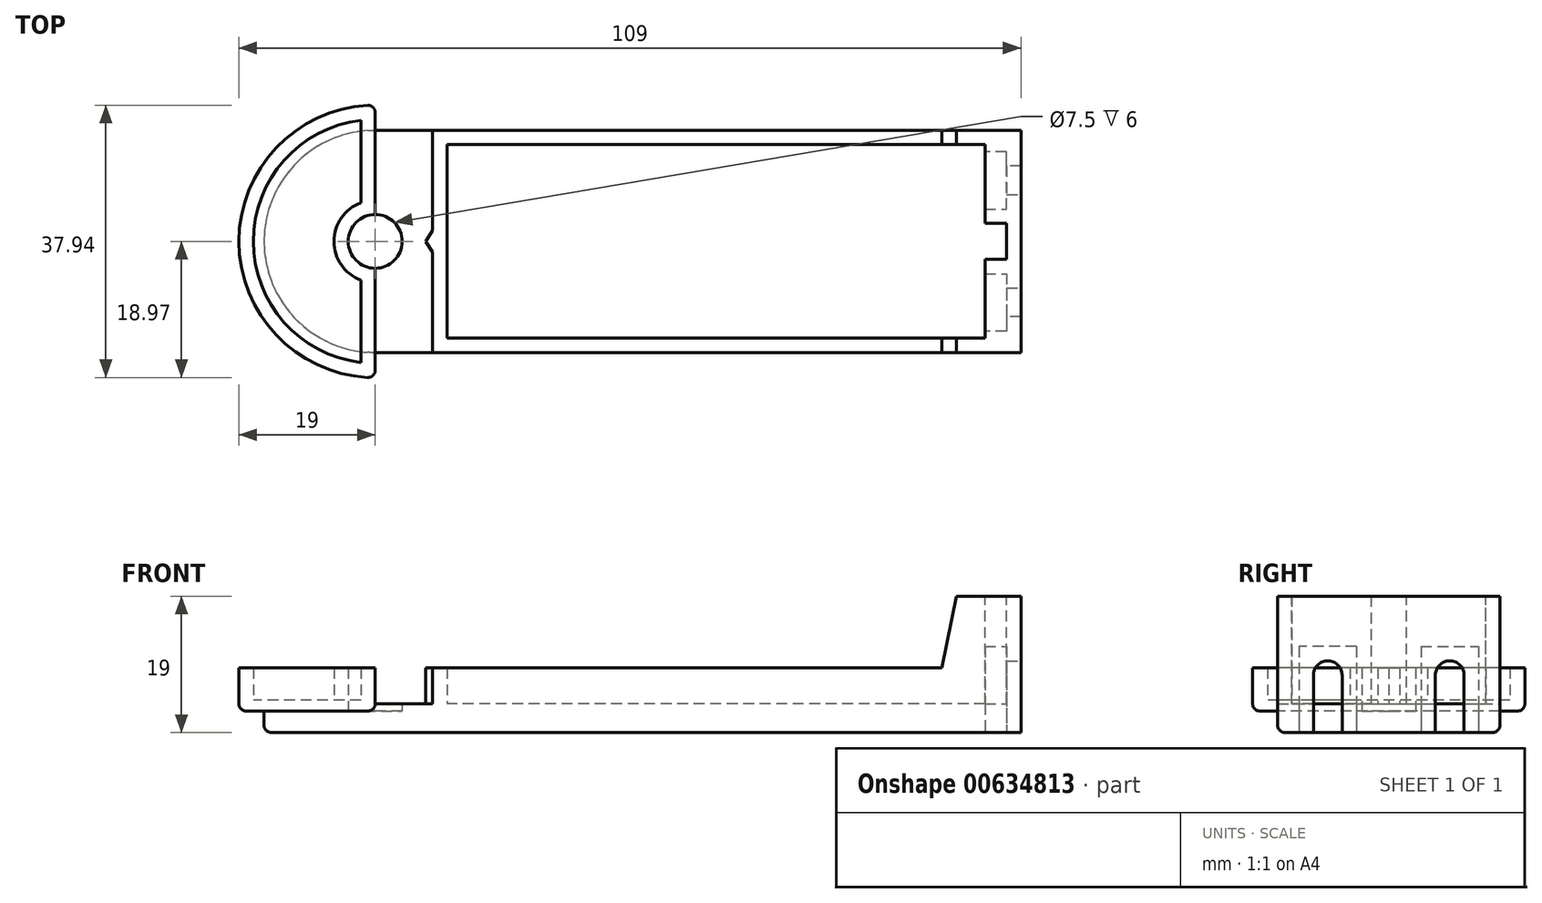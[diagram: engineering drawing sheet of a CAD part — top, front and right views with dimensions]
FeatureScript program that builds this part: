
annotation { "Feature Type Name" : "Feature", "Feature Type Description" : "" }
export const myFeature = defineFeature(function(context is Context, id is Id, definition is map)
    precondition{}
    {
        {
            var Q0;
            Q0=qCreatedBy(makeId("Top.planeOp"),FACE);
            var sketch = newSketch(context, id + "F0", { "sketchPlane" : qUnion([Q0])});
            skCircle(sketch, "E0", {"center": v(0, 0) * mm, "radius": 15.5 * mm});
            skLineSegment(sketch, "E1.bottom", {"start": v(0, 15.5) * mm, "end": v(90, 15.5) * mm});
            skLineSegment(sketch, "E1.top", {"start": v(0, -15.5) * mm, "end": v(90, -15.5) * mm});
            skLineSegment(sketch, "E1.left", {"start": v(0, 15.5) * mm, "end": v(0, -15.5) * mm});
            skLineSegment(sketch, "E1.right", {"start": v(90, 15.5) * mm, "end": v(90, -15.5) * mm});
            skSolve(sketch);
        }
        {
            var Q0;
            Q0 = qSketchRegion(id + "F0", true);
            extrude(context, id + "F1", {"entities" : qUnion([Q0]), "depth" : 4 * mm, "offsetDistance" : 25 * mm});
        }
        {
            var Q0;
            Q0=makeQuery(id+"F1.opExtrude","CAP_FACE",FACE,{"disambiguationData":[OSD([sQuery(id+"F0.wireOp",EDGE,"E0"),sQuery(id+"F0.wireOp",EDGE,"E1.bottom"),sQuery(id+"F0.wireOp",EDGE,"E1.top"),sQuery(id+"F0.wireOp",EDGE,"E1.right")])],"isStart":false});
            var sketch = newSketch(context, id + "F2", { "sketchPlane" : qUnion([Q0])});
            skLineSegment(sketch, "E2.top", {"start": v(90, 15.5) * mm, "end": v(8, 15.5) * mm});
            skLineSegment(sketch, "E2.left", {"start": v(90, -15.5) * mm, "end": v(90, 15.5) * mm});
            skLineSegment(sketch, "E3.0", {"start": v(88, 13.5) * mm, "end": v(10, 13.5) * mm});
            skLineSegment(sketch, "E4.0", {"start": v(88, -13.5) * mm, "end": v(88, 13.5) * mm});
            skLineSegment(sketch, "E5", {"start": v(90, -15.5) * mm, "end": v(8, -15.5) * mm});
            skLineSegment(sketch, "E6", {"start": v(10, -13.5) * mm, "end": v(88, -13.5) * mm});
            skLineSegment(sketch, "E7", {"start": v(8, -15.5) * mm, "end": v(8, 15.5) * mm});
            skLineSegment(sketch, "E8.0", {"start": v(10, -13.5) * mm, "end": v(10, 13.5) * mm});
            skSolve(sketch);
        }
        {
            var Q0;
            Q0 = qSketchRegion(id + "F2", true);
            extrude(context, id + "F3", {"entities" : qUnion([Q0]), "operationType" : NewBodyOperationType.ADD, "depth" : 15 * mm, "offsetDistance" : 25 * mm});
        }
        {
            var Q0;
            Q0=makeQuery(id+"F3.boolean.opBoolean","MERGE",FACE,{"derivedFrom":[makeQuery(id+"F1.opExtrude","SWEPT_FACE",FACE,{"disambiguationData":[OSD([sQuery(id+"F0.wireOp",EDGE,"E1.top")])]}),makeQuery(id+"F3.opExtrude","SWEPT_FACE",FACE,{"disambiguationData":[OSD([sQuery(id+"F2.wireOp",EDGE,"E2.bottom")])]})]});
            var sketch = newSketch(context, id + "F4", { "sketchPlane" : qUnion([Q0])});
            skLineSegment(sketch, "E9", {"start": v(79, 9) * mm, "end": v(81, 19) * mm});
            skLineSegment(sketch, "E10", {"start": v(8, 9) * mm, "end": v(8, 19) * mm});
            skLineSegment(sketch, "E11", {"start": v(81, 19) * mm, "end": v(8, 19) * mm});
            skLineSegment(sketch, "E12", {"start": v(8, 9) * mm, "end": v(79, 9) * mm});
            skSolve(sketch);
        }
        {
            var Q0;
            Q0 = qSketchRegion(id + "F4", true);
            extrude(context, id + "F5", {"entities" : qUnion([Q0]), "operationType" : NewBodyOperationType.REMOVE, "oppositeDirection" : true, "depth" : 31 * mm, "offsetDistance" : 25 * mm});
        }
        {
            var Q0;
            Q0=makeQuery(id+"F1.opExtrude","CAP_FACE",FACE,{"disambiguationData":[OSD([sQuery(id+"F0.wireOp",EDGE,"E0"),sQuery(id+"F0.wireOp",EDGE,"E1.bottom"),sQuery(id+"F0.wireOp",EDGE,"E1.top"),sQuery(id+"F0.wireOp",EDGE,"E1.right")])],"isStart":true});
            var sketch = newSketch(context, id + "F6", { "sketchPlane" : qUnion([Q0])});
            skLineSegment(sketch, "E13.bottom", {"start": v(90, 15.5) * mm, "end": v(85, 15.5) * mm});
            skLineSegment(sketch, "E13.top", {"start": v(90, 2.5) * mm, "end": v(85, 2.5) * mm});
            skLineSegment(sketch, "E13.left", {"start": v(90, 15.5) * mm, "end": v(90, 2.5) * mm});
            skLineSegment(sketch, "E13.right", {"start": v(85, 15.5) * mm, "end": v(85, 2.5) * mm});
            skLineSegment(sketch, "E14.bottom", {"start": v(90, -15.5) * mm, "end": v(85, -15.5) * mm});
            skLineSegment(sketch, "E14.top", {"start": v(90, -2.5) * mm, "end": v(85, -2.5) * mm});
            skLineSegment(sketch, "E14.left", {"start": v(90, -15.5) * mm, "end": v(90, -2.5) * mm});
            skLineSegment(sketch, "E14.right", {"start": v(85, -15.5) * mm, "end": v(85, -2.5) * mm});
            skSolve(sketch);
        }
        {
            var Q0;
            Q0 = qSketchRegion(id + "F6", true);
            extrude(context, id + "F7", {"entities" : qUnion([Q0]), "operationType" : NewBodyOperationType.ADD, "oppositeDirection" : true, "depth" : 19 * mm, "offsetDistance" : 25 * mm});
        }
        {
            var Q0;
            Q0=makeQuery(id+"F1.opExtrude","CAP_FACE",FACE,{"disambiguationData":[OSD([sQuery(id+"F0.wireOp",EDGE,"E0"),sQuery(id+"F0.wireOp",EDGE,"E1.bottom"),sQuery(id+"F0.wireOp",EDGE,"E1.top"),sQuery(id+"F0.wireOp",EDGE,"E1.right")])],"isStart":true});
            var sketch = newSketch(context, id + "F8", { "sketchPlane" : qUnion([Q0])});
            skLineSegment(sketch, "E15", {"start": v(90, -15.5) * mm, "end": v(90, -10.5) * mm});
            skLineSegment(sketch, "E16", {"start": v(90, -10.5) * mm, "end": v(88, -10.5) * mm});
            skLineSegment(sketch, "E17", {"start": v(88, -10.5) * mm, "end": v(88, -12.5) * mm});
            skLineSegment(sketch, "E18", {"start": v(88, -12.5) * mm, "end": v(85, -12.5) * mm});
            skLineSegment(sketch, "E19", {"start": v(85, -12.5) * mm, "end": v(85, -4.5) * mm});
            skLineSegment(sketch, "E20", {"start": v(85, -4.5) * mm, "end": v(88, -4.5) * mm});
            skLineSegment(sketch, "E21", {"start": v(88, -4.5) * mm, "end": v(88, -6.5) * mm});
            skLineSegment(sketch, "E22", {"start": v(88, -6.5) * mm, "end": v(90, -6.5) * mm});
            skLineSegment(sketch, "E23", {"start": v(90, -6.5) * mm, "end": v(90, -10.5) * mm});
            skLineSegment(sketch, "E24", {"start": v(0, 0) * mm, "end": v(90, 0) * mm, "construction": true});
            skLineSegment(sketch, "E25.MirrorCS", {"start": v(90, 6.5) * mm, "end": v(90, 10.5) * mm});
            skLineSegment(sketch, "E26.MirrorCS", {"start": v(88, 6.5) * mm, "end": v(90, 6.5) * mm});
            skLineSegment(sketch, "E27.MirrorCS", {"start": v(90, 15.5) * mm, "end": v(90, 10.5) * mm});
            skLineSegment(sketch, "E28.MirrorCS", {"start": v(88, 4.5) * mm, "end": v(88, 6.5) * mm});
            skLineSegment(sketch, "E29.MirrorCS", {"start": v(90, 10.5) * mm, "end": v(88, 10.5) * mm});
            skLineSegment(sketch, "E30.MirrorCS", {"start": v(88, 12.5) * mm, "end": v(85, 12.5) * mm});
            skLineSegment(sketch, "E31.MirrorCS", {"start": v(88, 10.5) * mm, "end": v(88, 12.5) * mm});
            skLineSegment(sketch, "E32.MirrorCS", {"start": v(85, 4.5) * mm, "end": v(88, 4.5) * mm});
            skLineSegment(sketch, "E33.MirrorCS", {"start": v(85, 12.5) * mm, "end": v(85, 4.5) * mm});
            skSolve(sketch);
        }
        {
            var Q0;
            Q0 = qSketchRegion(id + "F8", true);
            extrude(context, id + "F9", {"entities" : qUnion([Q0]), "operationType" : NewBodyOperationType.REMOVE, "oppositeDirection" : true, "depth" : 12 * mm, "offsetDistance" : 25 * mm});
        }
        {
            var Q0;
            Q0=makeQuery(id+"F3.boolean.opBoolean","MERGE",FACE,{"derivedFrom":[makeQuery(id+"F1.opExtrude","SWEPT_FACE",FACE,{"disambiguationData":[OSD([sQuery(id+"F0.wireOp",EDGE,"E1.right")])]}),makeQuery(id+"F3.opExtrude","SWEPT_FACE",FACE,{"disambiguationData":[OSD([sQuery(id+"F2.wireOp",EDGE,"E2.left")])]})]});
            var sketch = newSketch(context, id + "F10", { "sketchPlane" : qUnion([Q0])});
            skLineSegment(sketch, "E34.bottom", {"start": v(10.5, 12) * mm, "end": v(6.5, 12) * mm});
            skLineSegment(sketch, "E34.left", {"start": v(10.5, 12) * mm, "end": v(10.5, 8) * mm});
            skLineSegment(sketch, "E34.right", {"start": v(6.5, 12) * mm, "end": v(6.5, 8) * mm});
            skLineSegment(sketch, "E35.bottom", {"start": v(-6.5, 12) * mm, "end": v(-10.5, 12) * mm});
            skLineSegment(sketch, "E35.left", {"start": v(-6.5, 12) * mm, "end": v(-6.5, 8) * mm});
            skLineSegment(sketch, "E35.right", {"start": v(-10.5, 12) * mm, "end": v(-10.5, 8) * mm});
            skArc(sketch, "E36", {"start": v(10.5, 8) * mm, "mid": v(8.5, 10) * mm, "end": v(6.5, 8) * mm});
            skArc(sketch, "E37", {"start": v(-6.5, 8) * mm, "mid": v(-8.5, 10) * mm, "end": v(-10.5, 8) * mm});
            skSolve(sketch);
        }
        {
            var Q0;
            Q0 = qSketchRegion(id + "F10", true);
            extrude(context, id + "F11", {"entities" : qUnion([Q0]), "operationType" : NewBodyOperationType.ADD, "oppositeDirection" : true, "depth" : 2 * mm, "offsetDistance" : 25 * mm});
        }
        {
            var Q0;
            {var subQ0=sQuery(id+"F0.wireOp",EDGE,"E1.top");var subQ1=sQuery(id+"F0.wireOp",EDGE,"E1.bottom");var subQ2=sQuery(id+"F0.wireOp",EDGE,"E0");Q0=makeQuery(id+"F3.boolean.opBoolean","SPLIT",FACE,{"disambiguationData":[TD([makeQuery(id+"F1.opExtrude","SWEPT_FACE",FACE,{"disambiguationData":[OSD([subQ2])]})])],"derivedFrom":makeQuery(id+"F1.opExtrude","CAP_FACE",FACE,{"disambiguationData":[OSD([subQ2,subQ1,subQ0,sQuery(id+"F0.wireOp",EDGE,"E1.right")])],"isStart":false})});}
            var sketch = newSketch(context, id + "F12", { "sketchPlane" : qUnion([Q0])});
            skArc(sketch, "E38", {"start": v(0, 3.75) * mm, "mid": v(-3.75, 0) * mm, "end": v(0, -3.75) * mm});
            skArc(sketch, "E39", {"start": v(-2, 16.88) * mm, "mid": v(-17, 0) * mm, "end": v(-2, -16.88) * mm});
            skArc(sketch, "E40", {"start": v(-1.06, 18.97) * mm, "mid": v(-19, 0) * mm, "end": v(-1.06, -18.97) * mm});
            skArc(sketch, "E41", {"start": v(-2, 5.4) * mm, "mid": v(-5.75, 0) * mm, "end": v(-2, -5.4) * mm});
            skLineSegment(sketch, "E42", {"start": v(0, 17.97) * mm, "end": v(0, 3.75) * mm});
            skLineSegment(sketch, "E43.0", {"start": v(-2, 19) * mm, "end": v(-2, 18.9) * mm});
            skLineSegment(sketch, "E44.trimOffspring", {"start": v(-2, -18.9) * mm, "end": v(-2, -19) * mm});
            skLineSegment(sketch, "E45.trimOffspring", {"start": v(-2, 16.88) * mm, "end": v(-2, 5.4) * mm});
            skLineSegment(sketch, "E46.trimOffspring", {"start": v(-2, -5.4) * mm, "end": v(-2, -16.88) * mm});
            skLineSegment(sketch, "E47.trimOffspring", {"start": v(0, -3.75) * mm, "end": v(0, -17.97) * mm});
            skPoint(sketch, "E48.visualSharp", {"position": v(0, 19) * mm});
            skArc(sketch, "E48.filletArc", {"start": v(0, 17.97) * mm, "mid": v(-0.31, 18.7) * mm, "end": v(-1.06, 18.97) * mm});
            skPoint(sketch, "E49.visualSharp", {"position": v(0, -19) * mm});
            skArc(sketch, "E49.filletArc", {"start": v(-1.06, -18.97) * mm, "mid": v(-0.31, -18.7) * mm, "end": v(0, -17.97) * mm});
            skSolve(sketch);
        }
        {
            var Q0;
            Q0 = qSketchRegion(id + "F12", true);
            extrude(context, id + "F13", {"entities" : qUnion([Q0]), "operationType" : NewBodyOperationType.ADD, "depth" : 5 * mm, "offsetDistance" : 25 * mm, "hasSecondDirection" : true, "secondDirectionOppositeDirection" : true, "secondDirectionDepth" : 1 * mm});
        }
        {
            var Q0;
            {var subQ0=sQuery(id+"F12.wireOp",EDGE,"E41");var subQ3=sQuery(id+"F0.wireOp",EDGE,"E0");var subQ4=makeQuery(id+"F1.opExtrude","SWEPT_FACE",FACE,{"disambiguationData":[OSD([subQ3])]});var subQ5=sQuery(id+"F0.wireOp",EDGE,"E1.top");var subQ6=sQuery(id+"F0.wireOp",EDGE,"E1.bottom");Q0=makeQuery(id+"F13.boolean.opBoolean","SPLIT",FACE,{"disambiguationData":[TD([makeQuery(id+"F13.opExtrude","SWEPT_FACE",FACE,{"disambiguationData":[OSD([subQ0])]})])],"derivedFrom":makeQuery(id+"F3.boolean.opBoolean","SPLIT",FACE,{"disambiguationData":[TD([subQ4])],"derivedFrom":makeQuery(id+"F1.opExtrude","CAP_FACE",FACE,{"disambiguationData":[OSD([subQ3,subQ6,subQ5,sQuery(id+"F0.wireOp",EDGE,"E1.right")])],"isStart":false})})});}
            var sketch = newSketch(context, id + "F14", { "sketchPlane" : qUnion([Q0])});
            skLineSegment(sketch, "E50.0", {"start": v(-2.01, 19.14) * mm, "end": v(-2.01, 19.03) * mm});
            skLineSegment(sketch, "E51.trimOffspring", {"start": v(-2.01, -19.03) * mm, "end": v(-2.01, -19.14) * mm});
            skLineSegment(sketch, "E52.trimOffspring", {"start": v(0, 17) * mm, "end": v(0, 5.75) * mm});
            skLineSegment(sketch, "E53.trimOffspring", {"start": v(0, -5.75) * mm, "end": v(0, -17) * mm});
            skArc(sketch, "E54", {"start": v(0, 17) * mm, "mid": v(-17, 0) * mm, "end": v(0, -17) * mm});
            skArc(sketch, "E55", {"start": v(0, 5.75) * mm, "mid": v(-5.75, 0) * mm, "end": v(0, -5.75) * mm});
            skSolve(sketch);
        }
        {
            var Q0;
            Q0 = qSketchRegion(id + "F14", true);
            extrude(context, id + "F15", {"entities" : qUnion([Q0]), "operationType" : NewBodyOperationType.ADD, "depth" : 0.5 * mm, "offsetDistance" : 25 * mm, "hasSecondDirection" : true, "secondDirectionOppositeDirection" : true, "secondDirectionDepth" : 1 * mm});
        }
        {
            var Q0;
            Q0=makeQuery(id+"F1.opExtrude","CAP_EDGE",EDGE,{"disambiguationData":[OSD([sQuery(id+"F0.wireOp",EDGE,"E1.top")])],"isStart":true});
            var Q1;
            Q1=makeQuery(id+"F13.opExtrude","CAP_EDGE",EDGE,{"disambiguationData":[OSD([sQuery(id+"F12.wireOp",EDGE,"E40")])],"isStart":true});
            fillet(context, id + "F16", {"entities" : qUnion([Q0, Q1]), "radius" : 1 * mm, "tangentPropagation" : true, "allowEdgeOverflow" : false});
        }
        {
            var Q0;
            {var subQ4=sQuery(id+"F12.wireOp",EDGE,"E38");Q0=makeQuery(id+"F12.imprint","IMPRINT",FACE,{"disambiguationData":[TD([[makeQuery(id+"F12.imprint","IMPRINT",EDGE,{"derivedFrom":subQ4}),1.0]])]});}
            var sketch = newSketch(context, id + "F17", { "sketchPlane" : qUnion([Q0])});
            skCircle(sketch, "E56", {"center": v(0, 0) * mm, "radius": 3.75 * mm});
            skSolve(sketch);
        }
        {
            var Q0;
            Q0 = qSketchRegion(id + "F17", true);
            extrude(context, id + "F18", {"entities" : qUnion([Q0]), "operationType" : NewBodyOperationType.REMOVE, "oppositeDirection" : true, "depth" : 1 * mm, "offsetDistance" : 25 * mm});
        }
        {
            var Q0;
            {var subQ4=sQuery(id+"F12.wireOp",EDGE,"E38");Q0=makeQuery(id+"F12.imprint","IMPRINT",FACE,{"disambiguationData":[TD([[makeQuery(id+"F12.imprint","IMPRINT",EDGE,{"derivedFrom":subQ4}),1.0]])]});}
            var sketch = newSketch(context, id + "F19", { "sketchPlane" : qUnion([Q0])});
            skLineSegment(sketch, "E57", {"start": v(8, -1.5) * mm, "end": v(7, 0) * mm});
            skLineSegment(sketch, "E58", {"start": v(7, 0) * mm, "end": v(8, 1.5) * mm});
            skLineSegment(sketch, "E59", {"start": v(8, 1.5) * mm, "end": v(8, -1.5) * mm});
            skSolve(sketch);
        }
        {
            var Q0;
            Q0 = qSketchRegion(id + "F19", true);
            extrude(context, id + "F20", {"entities" : qUnion([Q0]), "operationType" : NewBodyOperationType.ADD, "depth" : 5 * mm, "offsetDistance" : 25 * mm});
        }
    });
